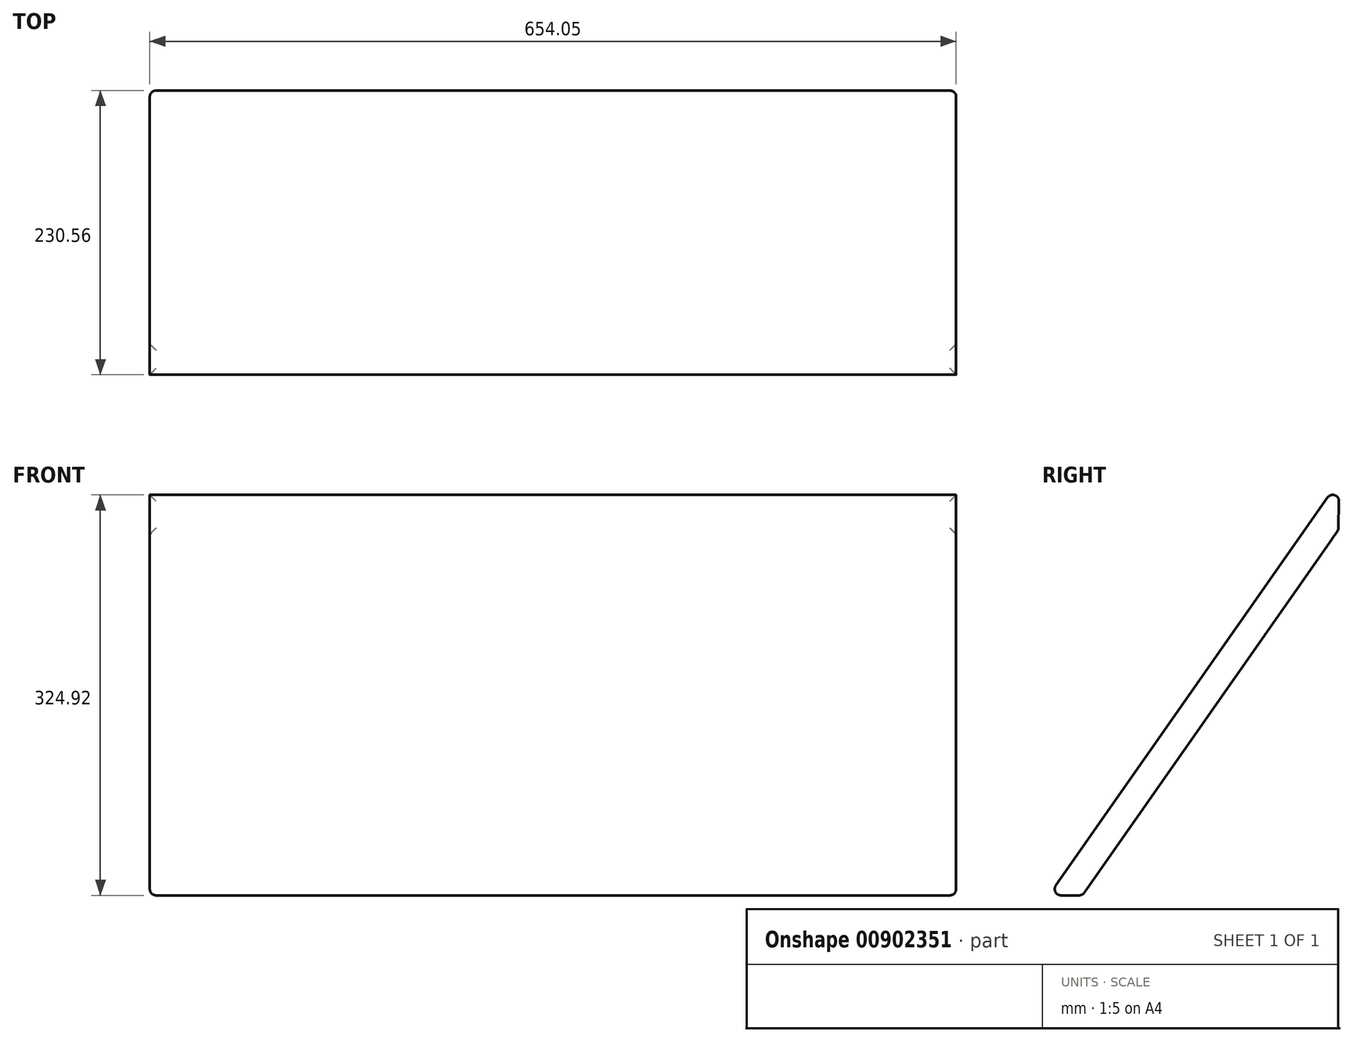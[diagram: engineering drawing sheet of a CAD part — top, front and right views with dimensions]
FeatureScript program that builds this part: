
annotation { "Feature Type Name" : "Feature", "Feature Type Description" : "" }
export const myFeature = defineFeature(function(context is Context, id is Id, definition is map)
    precondition{}
    {
        {
            var Q0;
            Q0=qCreatedBy(makeId("Right.planeOp"),FACE);
            var sketch = newSketch(context, id + "F0", { "sketchPlane" : qUnion([Q0])});
            skLineSegment(sketch, "E0", {"start": v(0, 0) * mm, "end": v(235.57, 336.43) * mm});
            skLineSegment(sketch, "E1", {"start": v(235.57, 336.43) * mm, "end": v(228.87, 0) * mm});
            skLineSegment(sketch, "E2", {"start": v(228.87, 0) * mm, "end": v(0, 0) * mm});
            skLineSegment(sketch, "E3", {"start": v(27.13, 0) * mm, "end": v(234.77, 296.54) * mm});
            skSolve(sketch);
        }
        {
            var Q0;
            {var subQ0=sQuery(id+"F0.wireOp",EDGE,"E0");Q0=makeQuery(id+"F0.imprint","IMPRINT",FACE,{"disambiguationData":[TD([[makeQuery(id+"F0.imprint","IMPRINT",EDGE,{"derivedFrom":subQ0}),-1.0]])]});}
            extrude(context, id + "F1", {"entities" : qUnion([Q0]), "oppositeDirection" : true, "depth" : 654.05 * mm, "offsetDistance" : 25.4 * mm});
        }
        {
            var Q0;
            Q0=makeQuery(id+"F1.opExtrude","SWEPT_FACE",FACE,{"disambiguationData":[OSD([sQuery(id+"F0.wireOp",EDGE,"E1")])]});
            var Q1;
            Q1=makeQuery(id+"F1.opExtrude","SWEPT_FACE",FACE,{"disambiguationData":[OSD([sQuery(id+"F0.wireOp",EDGE,"E2")])]});
            fillet(context, id + "F2", {"entities" : qUnion([Q0, Q1]), "radius" : 5.08 * mm, "tangentPropagation" : true, "allowEdgeOverflow" : false});
        }
    });
